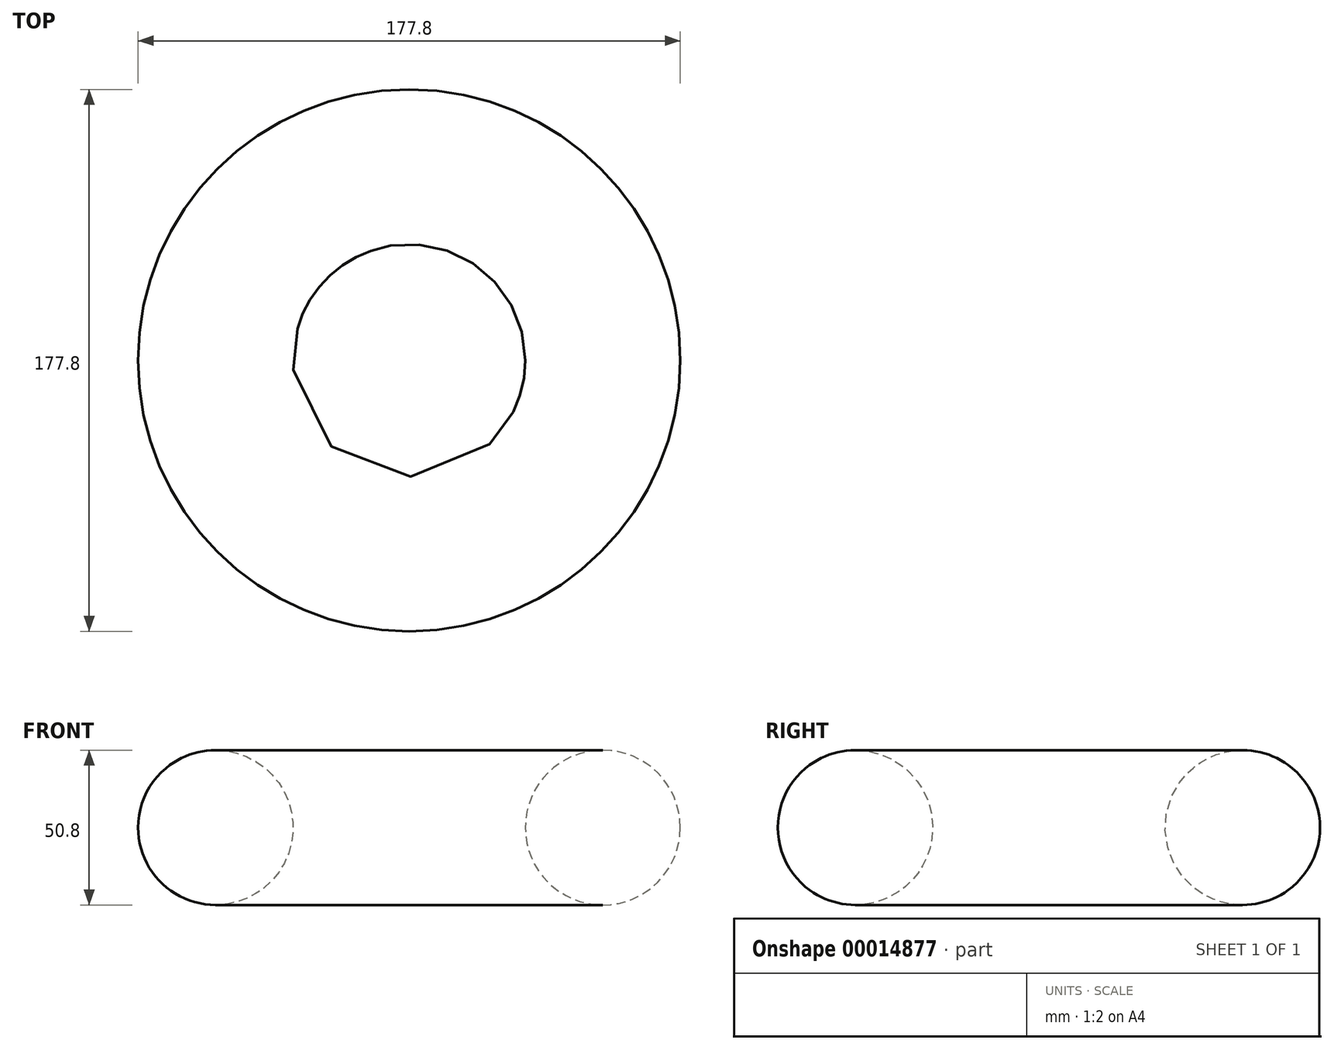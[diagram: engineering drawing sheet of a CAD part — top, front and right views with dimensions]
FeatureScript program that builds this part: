
annotation { "Feature Type Name" : "Feature", "Feature Type Description" : "" }
export const myFeature = defineFeature(function(context is Context, id is Id, definition is map)
    precondition{}
    {
        {
            var Q0;
            Q0=qCreatedBy(makeId("Top.planeOp"),FACE);
            var sketch = newSketch(context, id + "F0", { "sketchPlane" : qUnion([Q0])});
            skCircle(sketch, "E0", {"center": v(0, 0) * mm, "radius": 63.5 * mm});
            skSolve(sketch);
        }
        {
            var Q0;
            Q0=qCreatedBy(makeId("Front.planeOp"),FACE);
            var sketch = newSketch(context, id + "F1", { "sketchPlane" : qUnion([Q0])});
            skCircle(sketch, "E1", {"center": v(63.5, 0) * mm, "radius": 25.4 * mm});
            skSolve(sketch);
        }
        {
            var Q0;
            Q0=makeQuery(id+"F1.imprint","IMPRINT",FACE,{"disambiguationData":[TD([[makeQuery(id+"F1.imprint","IMPRINT",EDGE,{"derivedFrom":sQuery(id+"F1.wireOp",EDGE,"E1")}),1.0]])]});
            var Q1;
            Q1=sQuery(id+"F0.wireOp",EDGE,"E0");
            sweep(context, id + "F2", {"profiles" : qUnion([Q0]), "path" : qUnion([Q1])});
        }
    });
